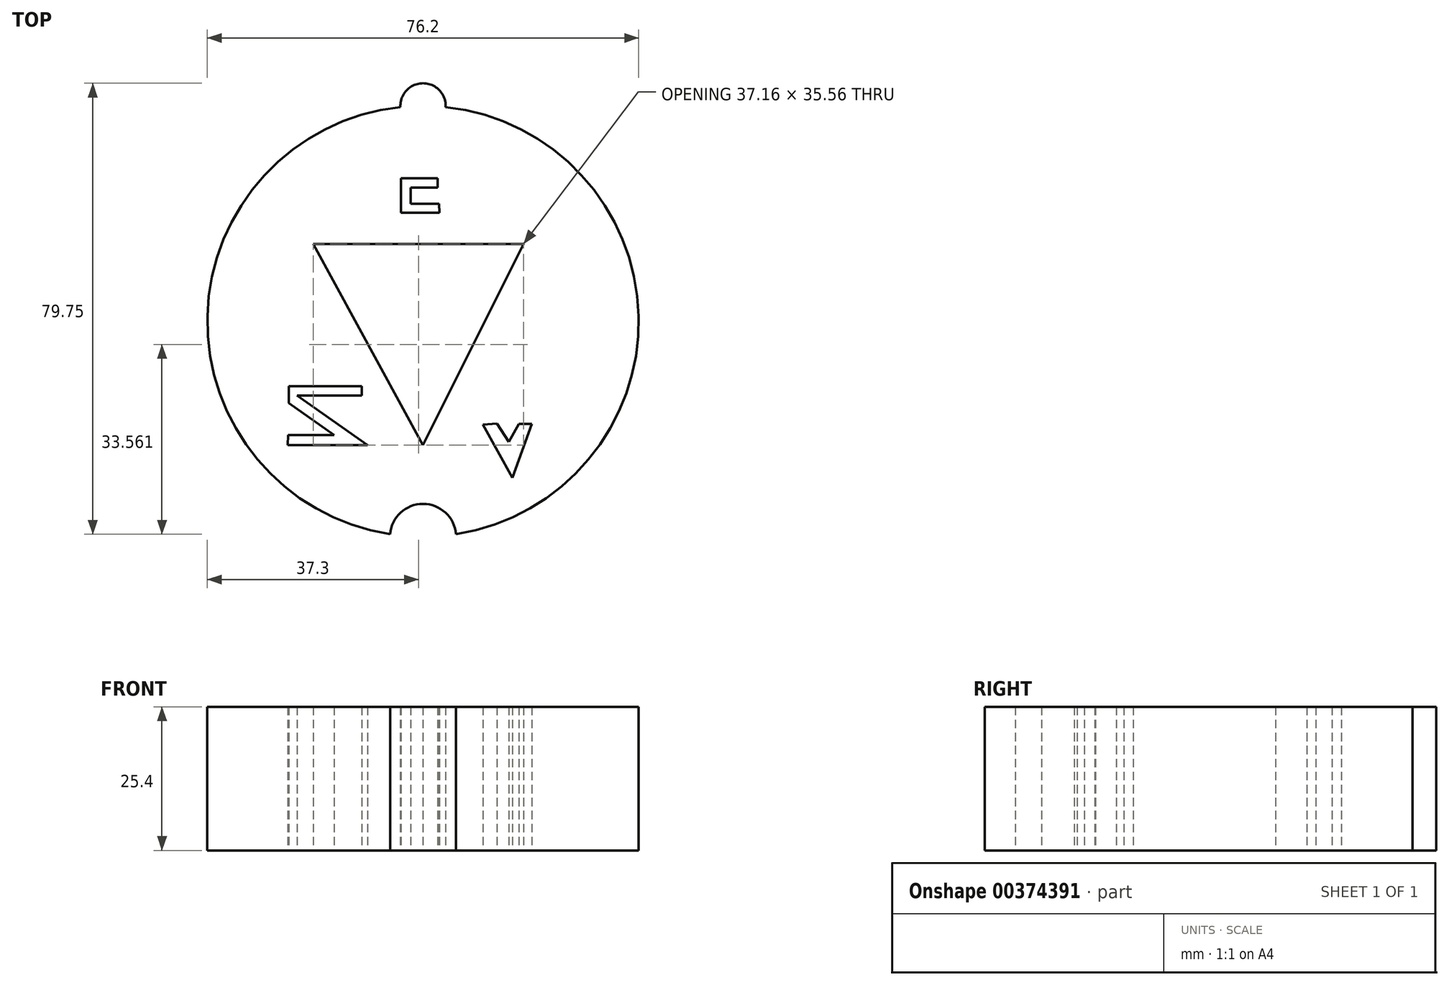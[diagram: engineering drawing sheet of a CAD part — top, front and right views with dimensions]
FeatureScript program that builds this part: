
annotation { "Feature Type Name" : "Feature", "Feature Type Description" : "" }
export const myFeature = defineFeature(function(context is Context, id is Id, definition is map)
    precondition{}
    {
        {
            var Q0;
            Q0=qCreatedBy(makeId("Front.planeOp"),FACE);
            var sketch = newSketch(context, id + "F0", { "sketchPlane" : qUnion([Q0])});
            skLineSegment(sketch, "E0", {"start": v(0, 0) * mm, "end": v(38.1, 0) * mm});
            skLineSegment(sketch, "E1", {"start": v(38.1, 0) * mm, "end": v(38.1, 25.4) * mm});
            skLineSegment(sketch, "E2", {"start": v(38.1, 25.4) * mm, "end": v(0, 25.4) * mm});
            skLineSegment(sketch, "E3", {"start": v(0, 25.4) * mm, "end": v(0, 0) * mm});
            skSolve(sketch);
        }
        {
            var Q0;
            Q0=makeQuery(id+"F0.imprint","IMPRINT",FACE,{"disambiguationData":[TD([[makeQuery(id+"F0.imprint","IMPRINT",EDGE,{"derivedFrom":sQuery(id+"F0.wireOp",EDGE,"E0")}),1.0]])]});
            var Q1;
            Q1=sQuery(id+"F0.wireOp",EDGE,"E3");
            revolve(context, id + "F1", {"entities" : qUnion([Q0]), "axis" : qUnion([Q1]), "revolveType" : RevolveType.FULL});
        }
        {
            var Q0;
            Q0=qCreatedBy(makeId("Top.planeOp"),FACE);
            var sketch = newSketch(context, id + "F2", { "sketchPlane" : qUnion([Q0])});
            skLineSegment(sketch, "E4", {"start": v(0, 0) * mm, "end": v(0, -21.87) * mm});
            skLineSegment(sketch, "E5", {"start": v(0, -21.87) * mm, "end": v(-19.38, 13.7) * mm});
            skLineSegment(sketch, "E6", {"start": v(-19.38, 13.7) * mm, "end": v(17.78, 13.7) * mm});
            skLineSegment(sketch, "E7", {"start": v(17.78, 13.7) * mm, "end": v(0, -21.87) * mm});
            skSolve(sketch);
        }
        {
            var Q0;
            Q0=makeQuery(id+"F2.imprint","IMPRINT",FACE,{"disambiguationData":[TD([[makeQuery(id+"F2.imprint","IMPRINT",EDGE,{"derivedFrom":sQuery(id+"F2.wireOp",EDGE,"E5")}),-1.0]])]});
            extrude(context, id + "F3", {"entities" : qUnion([Q0]), "operationType" : NewBodyOperationType.REMOVE, "depth" : 73.9 * mm});
        }
        {
            var Q0;
            Q0=makeQuery(id+"F1.opRevolve","SWEPT_FACE",FACE,{"disambiguationData":[OSD([sQuery(id+"F0.wireOp",EDGE,"E0")])]});
            var sketch = newSketch(context, id + "F4", { "sketchPlane" : qUnion([Q0])});
            skLineSegment(sketch, "E8", {"start": v(-23.9, 21.87) * mm, "end": v(-9.82, 21.87) * mm});
            skLineSegment(sketch, "E9", {"start": v(-9.82, 21.87) * mm, "end": v(-22.25, 13.1) * mm});
            skLineSegment(sketch, "E10", {"start": v(-22.25, 13.1) * mm, "end": v(-10.83, 13.1) * mm});
            skLineSegment(sketch, "E11", {"start": v(-10.83, 13.1) * mm, "end": v(-10.83, 11.45) * mm});
            skLineSegment(sketch, "E12", {"start": v(-23.73, 11.45) * mm, "end": v(-10.83, 11.45) * mm});
            skLineSegment(sketch, "E13", {"start": v(-23.73, 11.45) * mm, "end": v(-23.73, 14.44) * mm});
            skLineSegment(sketch, "E14", {"start": v(-23.73, 14.44) * mm, "end": v(-15.7, 20.1) * mm});
            skLineSegment(sketch, "E15", {"start": v(-15.7, 20.1) * mm, "end": v(-23.86, 20.1) * mm});
            skLineSegment(sketch, "E16", {"start": v(-23.86, 20.1) * mm, "end": v(-23.9, 21.87) * mm});
            skSolve(sketch);
        }
        {
            var Q0;
            Q0=makeQuery(id+"F4.imprint","IMPRINT",FACE,{"disambiguationData":[TD([[makeQuery(id+"F4.imprint","IMPRINT",EDGE,{"derivedFrom":sQuery(id+"F4.wireOp",EDGE,"E8")}),-1.0]])]});
            extrude(context, id + "F5", {"entities" : qUnion([Q0]), "operationType" : NewBodyOperationType.REMOVE, "oppositeDirection" : true, "depth" : 25.4 * mm});
        }
        {
            var Q0;
            Q0=makeQuery(id+"F1.opRevolve","SWEPT_FACE",FACE,{"disambiguationData":[OSD([sQuery(id+"F0.wireOp",EDGE,"E0")])]});
            var sketch = newSketch(context, id + "F6", { "sketchPlane" : qUnion([Q0])});
            skLineSegment(sketch, "E17", {"start": v(10.57, 18.26) * mm, "end": v(15.77, 27.66) * mm});
            skLineSegment(sketch, "E18", {"start": v(15.77, 27.66) * mm, "end": v(19.25, 18.1) * mm});
            skLineSegment(sketch, "E19", {"start": v(19.25, 18.1) * mm, "end": v(16.95, 18.1) * mm});
            skLineSegment(sketch, "E20", {"start": v(16.95, 18.1) * mm, "end": v(15.18, 21.33) * mm});
            skLineSegment(sketch, "E21", {"start": v(15.18, 21.33) * mm, "end": v(13.06, 18.1) * mm});
            skLineSegment(sketch, "E22", {"start": v(13.06, 18.1) * mm, "end": v(10.57, 18.26) * mm});
            skSolve(sketch);
        }
        {
            var Q0;
            Q0=makeQuery(id+"F6.imprint","IMPRINT",FACE,{"disambiguationData":[TD([[makeQuery(id+"F6.imprint","IMPRINT",EDGE,{"derivedFrom":sQuery(id+"F6.wireOp",EDGE,"E17")}),-1.0]])]});
            extrude(context, id + "F7", {"entities" : qUnion([Q0]), "operationType" : NewBodyOperationType.REMOVE, "oppositeDirection" : true, "depth" : 25.4 * mm});
        }
        {
            var Q0;
            Q0=makeQuery(id+"F1.opRevolve","SWEPT_FACE",FACE,{"disambiguationData":[OSD([sQuery(id+"F0.wireOp",EDGE,"E0")])]});
            var sketch = newSketch(context, id + "F8", { "sketchPlane" : qUnion([Q0])});
            skLineSegment(sketch, "E23", {"start": v(2.91, -19.23) * mm, "end": v(-3.89, -19.23) * mm});
            skLineSegment(sketch, "E24", {"start": v(-3.89, -19.23) * mm, "end": v(-3.89, -25.33) * mm});
            skLineSegment(sketch, "E25", {"start": v(-3.89, -25.33) * mm, "end": v(2.59, -25.33) * mm});
            skLineSegment(sketch, "E26", {"start": v(2.59, -25.33) * mm, "end": v(2.59, -23.64) * mm});
            skLineSegment(sketch, "E27", {"start": v(2.59, -23.64) * mm, "end": v(-2.18, -23.64) * mm});
            skLineSegment(sketch, "E28", {"start": v(-2.18, -23.64) * mm, "end": v(-2.18, -20.8) * mm});
            skLineSegment(sketch, "E29", {"start": v(-2.18, -20.8) * mm, "end": v(2.82, -20.8) * mm});
            skLineSegment(sketch, "E30", {"start": v(2.82, -20.8) * mm, "end": v(2.91, -19.23) * mm});
            skSolve(sketch);
        }
        {
            var Q0;
            Q0=makeQuery(id+"F8.imprint","IMPRINT",FACE,{"disambiguationData":[TD([[makeQuery(id+"F8.imprint","IMPRINT",EDGE,{"derivedFrom":sQuery(id+"F8.wireOp",EDGE,"E23")}),1.0]])]});
            extrude(context, id + "F9", {"entities" : qUnion([Q0]), "operationType" : NewBodyOperationType.REMOVE, "oppositeDirection" : true, "depth" : 25.4 * mm});
        }
        {
            var Q0;
            Q0=makeQuery(id+"F1.opRevolve","SWEPT_FACE",FACE,{"disambiguationData":[OSD([sQuery(id+"F0.wireOp",EDGE,"E0")])]});
            var sketch = newSketch(context, id + "F10", { "sketchPlane" : qUnion([Q0])});
            skCircle(sketch, "E31", {"center": v(0, 38.1) * mm, "radius": 5.83 * mm});
            skSolve(sketch);
        }
        {
            var Q0;
            {var subQ0=sQuery(id+"F10.wireOp",EDGE,"E31");var subQ1=makeQuery(id+"F1.opRevolve","SWEPT_EDGE",EDGE,{"disambiguationData":[OSD([sQuery(id+"F0.wireOp",EDGE,"E0"),sQuery(id+"F0.wireOp",EDGE,"E1")])]});var subQ2=makeQuery(id+"F10.imprint","INTERSECT",VERTEX,{"disambiguationData":[OD(0.0)],"derivedFrom":[subQ1,subQ0]});Q0=makeQuery(id+"F10.imprint","IMPRINT",FACE,{"disambiguationData":[TD([[makeQuery(id+"F10.imprint","IMPRINT",EDGE,{"disambiguationData":[TD([[subQ2,1.0]])],"derivedFrom":subQ0}),1.0]])]});}
            var Q1;
            {var subQ0=sQuery(id+"F10.wireOp",EDGE,"E31");var subQ1=makeQuery(id+"F1.opRevolve","SWEPT_EDGE",EDGE,{"disambiguationData":[OSD([sQuery(id+"F0.wireOp",EDGE,"E0"),sQuery(id+"F0.wireOp",EDGE,"E1")])]});var subQ2=makeQuery(id+"F10.imprint","INTERSECT",VERTEX,{"disambiguationData":[OD(0.0)],"derivedFrom":[subQ1,subQ0]});Q1=makeQuery(id+"F10.imprint","IMPRINT",FACE,{"disambiguationData":[TD([[makeQuery(id+"F10.imprint","IMPRINT",EDGE,{"disambiguationData":[TD([[subQ2,-1.0]])],"derivedFrom":subQ0}),1.0]])]});}
            extrude(context, id + "F11", {"entities" : qUnion([Q0, Q1]), "operationType" : NewBodyOperationType.REMOVE, "oppositeDirection" : true, "depth" : 25.4 * mm});
        }
        {
            var Q0;
            Q0=makeQuery(id+"F1.opRevolve","SWEPT_FACE",FACE,{"disambiguationData":[OSD([sQuery(id+"F0.wireOp",EDGE,"E0")])]});
            var sketch = newSketch(context, id + "F12", { "sketchPlane" : qUnion([Q0])});
            skCircle(sketch, "E32", {"center": v(0, -38.1) * mm, "radius": 4 * mm});
            skSolve(sketch);
        }
        {
            var Q0;
            {var subQ0=sQuery(id+"F12.wireOp",EDGE,"E32");var subQ1=makeQuery(id+"F1.opRevolve","SWEPT_EDGE",EDGE,{"disambiguationData":[OSD([sQuery(id+"F0.wireOp",EDGE,"E0"),sQuery(id+"F0.wireOp",EDGE,"E1")])]});var subQ2=makeQuery(id+"F12.imprint","INTERSECT",VERTEX,{"disambiguationData":[OD(0.0)],"derivedFrom":[subQ1,subQ0]});Q0=makeQuery(id+"F12.imprint","IMPRINT",FACE,{"disambiguationData":[TD([[makeQuery(id+"F12.imprint","IMPRINT",EDGE,{"disambiguationData":[TD([[subQ2,1.0]])],"derivedFrom":subQ0}),1.0]])]});}
            var Q1;
            {var subQ0=sQuery(id+"F12.wireOp",EDGE,"E32");var subQ1=makeQuery(id+"F1.opRevolve","SWEPT_EDGE",EDGE,{"disambiguationData":[OSD([sQuery(id+"F0.wireOp",EDGE,"E0"),sQuery(id+"F0.wireOp",EDGE,"E1")])]});var subQ2=makeQuery(id+"F12.imprint","INTERSECT",VERTEX,{"disambiguationData":[OD(0.0)],"derivedFrom":[subQ1,subQ0]});Q1=makeQuery(id+"F12.imprint","IMPRINT",FACE,{"disambiguationData":[TD([[makeQuery(id+"F12.imprint","IMPRINT",EDGE,{"disambiguationData":[TD([[subQ2,-1.0]])],"derivedFrom":subQ0}),1.0]])]});}
            extrude(context, id + "F13", {"entities" : qUnion([Q0, Q1]), "operationType" : NewBodyOperationType.ADD, "oppositeDirection" : true, "depth" : 25.4 * mm});
        }
    });
